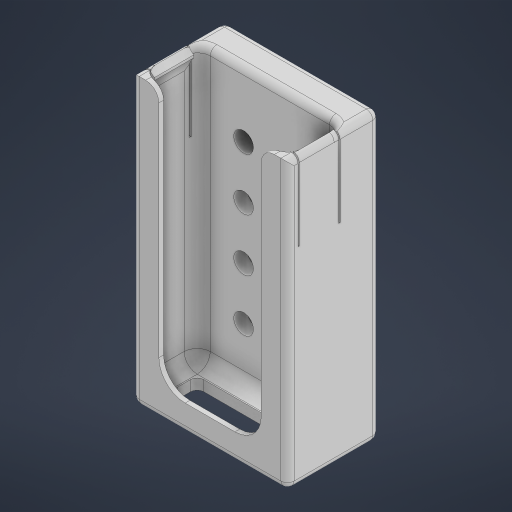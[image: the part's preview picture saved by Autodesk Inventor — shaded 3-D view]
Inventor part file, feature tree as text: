
AUTODESK INVENTOR PART (.ipt)
format: ipt  version: 2023 (Build 270158000, 158)  size: 409,088 bytes
history: native  units: in
note: dims shown in document units (in); Inventor stores cm internally (conversion verified against a paired STEP export)
features: sketch x7, extrude x6, fillet x4, projected_geometry x2, mirror x1, hole x1, pattern_linear x1
ambient origin geometry x8: Origin, YZ Plane, XZ Plane, XY Plane, X Axis, Y Axis, Z Axis, Center Point
bodies: Solid1 (feature_tree)
feature tree (22):
  extrude  "Extrusion1"  Depth=5.25in
  extrude  "Extrusion2"  Depth=1.75in TaperAngle=0.0deg
  extrude  "Extrusion3"  Depth=0.09in
  fillet  "Fillet1"  Radius=0.09in
  extrude  "Extrusion4"  Depth=5.25in TaperAngle=0.0deg
  extrude  "Extrusion5"  Depth=0.5in
  mirror  "Mirror1"
  extrude  "Extrusion6"  Depth=5.25in TaperAngle=0.0deg
  hole  "Hole1"  [1 undecoded]
  pattern_linear  "Rectangular Pattern1"  Spacing1=0.025in  [1 undecoded]
  fillet  "Fillet2"  Radius=0.025in
  fillet  "Fillet3"  Radius=0.75in
  fillet  "Fillet4"  Radius=1.5in
  sketch  "Sketch1"  dims[d0=2.75in d1=5.25in]
  sketch  "Sketch2"  dims[d2=0.1in d3=1.75in d4=0.0in]
  sketch  "Sketch3"  dims[d5=0.09in d6=0.09in d7=0.09in]
  sketch  "Sketch4"  dims[d8=1.05in d9=5.25in d10=0.0in]
  sketch  "Sketch5"  dims[d11=0.5in d12=0.5in]
  projected_geometry  "Projected Loop1"
  sketch  "Sketch6"  dims[d13=0.5in d14=5.25in d15=0.0in]
  projected_geometry  "Projected Loop2"
  sketch  "Sketch7"  dims[d16=0.25in d17=0.2in d18=0.025in d19=0.025in d20=0.75in d21=1.5in d22=0.0in d23=0.0in d30=1.0in d31=0.0in d32=0.1in d33=0.05in d35=0.375in d36=0.375in d37=0.1in d38=0.025in d39=1.0in d40=0.0in d42=0.5in d43=1.5in d44=0.156in d45=0.38in d46=0.375in d47=0.25in d48=0.5635in d49=1.0in d50=0.8108in d51=0.7874in d53=1.0in d54=1.5748in d56=1.0in d57=0.5in d58=0.25in d59=0.125in d60=0.375in]
note: 2 required parameter values undecoded (feature->parameter linkage not recoverable at this tier; creation-order binding heuristic only, values carry confidence <= 0.55)
